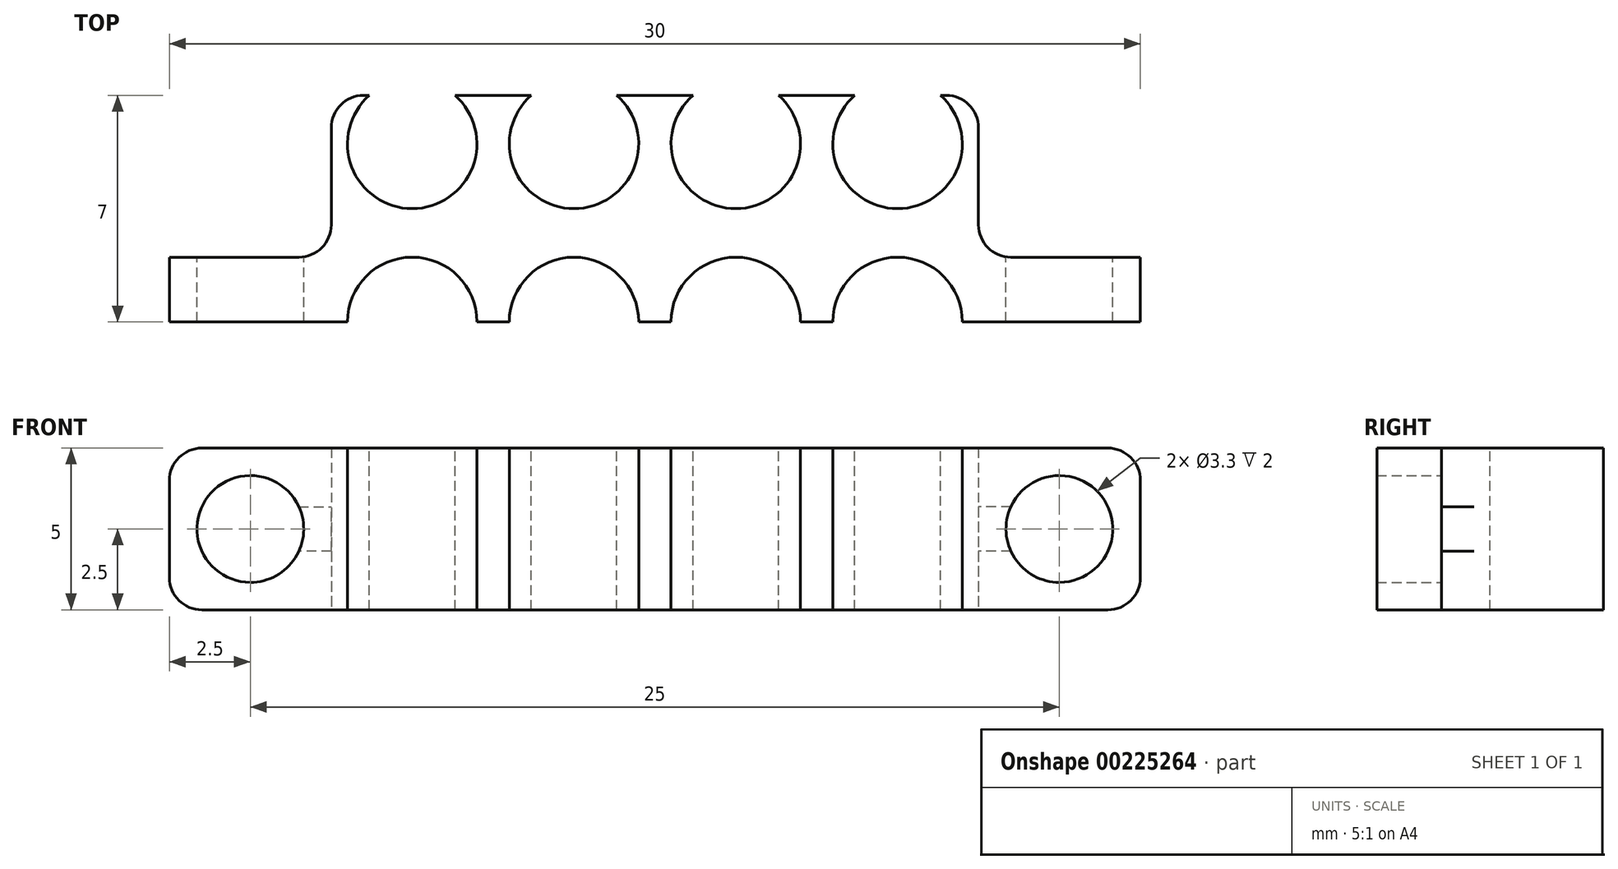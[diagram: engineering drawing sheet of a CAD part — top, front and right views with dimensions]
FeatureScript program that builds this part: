
annotation { "Feature Type Name" : "Feature", "Feature Type Description" : "" }
export const myFeature = defineFeature(function(context is Context, id is Id, definition is map)
    precondition{}
    {
        {
            var Q0;
            Q0=qCreatedBy(makeId("Top.planeOp"),FACE);
            var sketch = newSketch(context, id + "F0", { "sketchPlane" : qUnion([Q0])});
            skLineSegment(sketch, "E0.bottom", {"start": v(-10, 5) * mm, "end": v(10, 5) * mm});
            skLineSegment(sketch, "E0.top", {"start": v(-10, -2) * mm, "end": v(10, -2) * mm});
            skLineSegment(sketch, "E0.left", {"start": v(-10, 5) * mm, "end": v(-10, 0) * mm});
            skLineSegment(sketch, "E0.right", {"start": v(10, 5) * mm, "end": v(10, 0) * mm});
            skLineSegment(sketch, "E1.bottom", {"start": v(-10, -2) * mm, "end": v(-15, -2) * mm});
            skLineSegment(sketch, "E1.top", {"start": v(-10, 0) * mm, "end": v(-15, 0) * mm});
            skLineSegment(sketch, "E1.right", {"start": v(-15, -2) * mm, "end": v(-15, 0) * mm});
            skLineSegment(sketch, "E2.bottom", {"start": v(10, -2) * mm, "end": v(15, -2) * mm});
            skLineSegment(sketch, "E2.top", {"start": v(10, 0) * mm, "end": v(15, 0) * mm});
            skLineSegment(sketch, "E2.right", {"start": v(15, -2) * mm, "end": v(15, 0) * mm});
            skSolve(sketch);
        }
        {
            var Q0;
            Q0 = qSketchRegion(id + "F0", true);
            extrude(context, id + "F1", {"entities" : qUnion([Q0]), "depth" : 5 * mm, "offsetDistance" : 25 * mm});
        }
        {
            var Q0;
            Q0=makeQuery(id+"F1.opExtrude","SWEPT_FACE",FACE,{"disambiguationData":[OSD([sQuery(id+"F0.wireOp",EDGE,"E1.top")])]});
            var sketch = newSketch(context, id + "F2", { "sketchPlane" : qUnion([Q0])});
            skCircle(sketch, "E3", {"center": v(-12.5, 2.5) * mm, "radius": 1.65 * mm});
            skCircle(sketch, "E4", {"center": v(12.5, 2.5) * mm, "radius": 1.65 * mm});
            skPoint(sketch, "E4.centerSnap0", {"position": v(15, 2.5) * mm});
            skSolve(sketch);
        }
        {
            var Q0;
            Q0 = qSketchRegion(id + "F2", true);
            extrude(context, id + "F3", {"entities" : qUnion([Q0]), "operationType" : NewBodyOperationType.REMOVE, "endBound" : BoundingType.THROUGH_ALL, "oppositeDirection" : true, "depth" : 25 * mm, "offsetDistance" : 25 * mm});
        }
        {
            var Q0;
            Q0=makeQuery(id+"F1.opExtrude","CAP_FACE",FACE,{"disambiguationData":[OSD([sQuery(id+"F0.wireOp",EDGE,"E0.bottom"),sQuery(id+"F0.wireOp",EDGE,"E0.top"),sQuery(id+"F0.wireOp",EDGE,"E0.left"),sQuery(id+"F0.wireOp",EDGE,"E0.right"),sQuery(id+"F0.wireOp",EDGE,"E1.bottom"),sQuery(id+"F0.wireOp",EDGE,"E1.top"),sQuery(id+"F0.wireOp",EDGE,"E1.right"),sQuery(id+"F0.wireOp",EDGE,"E2.bottom"),sQuery(id+"F0.wireOp",EDGE,"E2.top"),sQuery(id+"F0.wireOp",EDGE,"E2.right")])],"isStart":false});
            var sketch = newSketch(context, id + "F4", { "sketchPlane" : qUnion([Q0])});
            skArc(sketch, "E5", {"start": v(-5.5, -2) * mm, "mid": v(-7.5, 0) * mm, "end": v(-9.5, -2) * mm});
            skArc(sketch, "E6.1.0.0", {"start": v(-0.5, -2) * mm, "mid": v(-2.5, 0) * mm, "end": v(-4.5, -2) * mm});
            skArc(sketch, "E6.2.0.0", {"start": v(4.5, -2) * mm, "mid": v(2.5, 0) * mm, "end": v(0.5, -2) * mm});
            skArc(sketch, "E6.3.0.0", {"start": v(9.5, -2) * mm, "mid": v(7.5, 0) * mm, "end": v(5.5, -2) * mm});
            skLineSegment(sketch, "E6.direction1", {"start": v(-9.5, -2) * mm, "end": v(-4.5, -2) * mm, "construction": true});
            skLineSegment(sketch, "E7", {"start": v(-12.27, 3.5) * mm, "end": v(13.45, 3.5) * mm, "construction": true});
            skCircle(sketch, "E8", {"center": v(-7.5, 3.5) * mm, "radius": 2 * mm});
            skPoint(sketch, "E8.centerSnap0", {"position": v(-7.5, 0) * mm});
            skCircle(sketch, "E9.1.0.0", {"center": v(-2.5, 3.5) * mm, "radius": 2 * mm});
            skCircle(sketch, "E9.2.0.0", {"center": v(2.5, 3.5) * mm, "radius": 2 * mm});
            skCircle(sketch, "E9.3.0.0", {"center": v(7.5, 3.5) * mm, "radius": 2 * mm});
            skLineSegment(sketch, "E9.direction1", {"start": v(-7.5, 3.5) * mm, "end": v(-2.5, 3.5) * mm, "construction": true});
            skSolve(sketch);
        }
        {
            var Q0;
            {var subQ0=sQuery(id+"F4.wireOp",EDGE,"E5");Q0=makeQuery(id+"F4.imprint","IMPRINT",FACE,{"disambiguationData":[TD([[makeQuery(id+"F4.imprint","IMPRINT",EDGE,{"derivedFrom":subQ0}),1.0]])]});}
            var Q1;
            {var subQ0=sQuery(id+"F4.wireOp",EDGE,"E6.1.0.0");Q1=makeQuery(id+"F4.imprint","IMPRINT",FACE,{"disambiguationData":[TD([[makeQuery(id+"F4.imprint","IMPRINT",EDGE,{"derivedFrom":subQ0}),1.0]])]});}
            var Q2;
            {var subQ0=sQuery(id+"F4.wireOp",EDGE,"E6.2.0.0");Q2=makeQuery(id+"F4.imprint","IMPRINT",FACE,{"disambiguationData":[TD([[makeQuery(id+"F4.imprint","IMPRINT",EDGE,{"derivedFrom":subQ0}),1.0]])]});}
            var Q3;
            {var subQ0=sQuery(id+"F4.wireOp",EDGE,"E6.3.0.0");Q3=makeQuery(id+"F4.imprint","IMPRINT",FACE,{"disambiguationData":[TD([[makeQuery(id+"F4.imprint","IMPRINT",EDGE,{"derivedFrom":subQ0}),1.0]])]});}
            var Q4;
            {var subQ0=sQuery(id+"F4.wireOp",EDGE,"E8");var subQ1=makeQuery(id+"F1.opExtrude","CAP_EDGE",EDGE,{"disambiguationData":[OSD([sQuery(id+"F0.wireOp",EDGE,"E0.bottom")])],"isStart":false});var subQ2=makeQuery(id+"F4.imprint","INTERSECT",VERTEX,{"disambiguationData":[OD(0.0)],"derivedFrom":[subQ1,subQ0]});Q4=makeQuery(id+"F4.imprint","IMPRINT",FACE,{"disambiguationData":[TD([[makeQuery(id+"F4.imprint","IMPRINT",EDGE,{"disambiguationData":[TD([[subQ2,1.0]])],"derivedFrom":subQ0}),1.0]])]});}
            var Q5;
            {var subQ0=sQuery(id+"F4.wireOp",EDGE,"E9.1.0.0");var subQ1=makeQuery(id+"F1.opExtrude","CAP_EDGE",EDGE,{"disambiguationData":[OSD([sQuery(id+"F0.wireOp",EDGE,"E0.bottom")])],"isStart":false});var subQ2=makeQuery(id+"F4.imprint","INTERSECT",VERTEX,{"disambiguationData":[OD(0.0)],"derivedFrom":[subQ1,subQ0]});Q5=makeQuery(id+"F4.imprint","IMPRINT",FACE,{"disambiguationData":[TD([[makeQuery(id+"F4.imprint","IMPRINT",EDGE,{"disambiguationData":[TD([[subQ2,1.0]])],"derivedFrom":subQ0}),1.0]])]});}
            var Q6;
            {var subQ0=sQuery(id+"F4.wireOp",EDGE,"E9.2.0.0");var subQ1=makeQuery(id+"F1.opExtrude","CAP_EDGE",EDGE,{"disambiguationData":[OSD([sQuery(id+"F0.wireOp",EDGE,"E0.bottom")])],"isStart":false});var subQ2=makeQuery(id+"F4.imprint","INTERSECT",VERTEX,{"disambiguationData":[OD(0.0)],"derivedFrom":[subQ1,subQ0]});Q6=makeQuery(id+"F4.imprint","IMPRINT",FACE,{"disambiguationData":[TD([[makeQuery(id+"F4.imprint","IMPRINT",EDGE,{"disambiguationData":[TD([[subQ2,-1.0]])],"derivedFrom":subQ0}),1.0]])]});}
            var Q7;
            {var subQ0=sQuery(id+"F4.wireOp",EDGE,"E9.3.0.0");var subQ1=makeQuery(id+"F1.opExtrude","CAP_EDGE",EDGE,{"disambiguationData":[OSD([sQuery(id+"F0.wireOp",EDGE,"E0.bottom")])],"isStart":false});var subQ2=makeQuery(id+"F4.imprint","INTERSECT",VERTEX,{"disambiguationData":[OD(0.0)],"derivedFrom":[subQ1,subQ0]});Q7=makeQuery(id+"F4.imprint","IMPRINT",FACE,{"disambiguationData":[TD([[makeQuery(id+"F4.imprint","IMPRINT",EDGE,{"disambiguationData":[TD([[subQ2,-1.0]])],"derivedFrom":subQ0}),1.0]])]});}
            var Q8;
            {var subQ0=sQuery(id+"F4.wireOp",EDGE,"E8");var subQ1=makeQuery(id+"F1.opExtrude","CAP_EDGE",EDGE,{"disambiguationData":[OSD([sQuery(id+"F0.wireOp",EDGE,"E0.bottom")])],"isStart":false});var subQ2=makeQuery(id+"F4.imprint","INTERSECT",VERTEX,{"disambiguationData":[OD(0.0)],"derivedFrom":[subQ1,subQ0]});Q8=makeQuery(id+"F4.imprint","IMPRINT",FACE,{"disambiguationData":[TD([[makeQuery(id+"F4.imprint","IMPRINT",EDGE,{"disambiguationData":[TD([[subQ2,-1.0]])],"derivedFrom":subQ0}),1.0]])]});}
            var Q9;
            {var subQ0=sQuery(id+"F4.wireOp",EDGE,"E9.1.0.0");var subQ1=makeQuery(id+"F1.opExtrude","CAP_EDGE",EDGE,{"disambiguationData":[OSD([sQuery(id+"F0.wireOp",EDGE,"E0.bottom")])],"isStart":false});var subQ2=makeQuery(id+"F4.imprint","INTERSECT",VERTEX,{"disambiguationData":[OD(0.0)],"derivedFrom":[subQ1,subQ0]});Q9=makeQuery(id+"F4.imprint","IMPRINT",FACE,{"disambiguationData":[TD([[makeQuery(id+"F4.imprint","IMPRINT",EDGE,{"disambiguationData":[TD([[subQ2,-1.0]])],"derivedFrom":subQ0}),1.0]])]});}
            var Q10;
            {var subQ0=sQuery(id+"F4.wireOp",EDGE,"E9.2.0.0");var subQ1=makeQuery(id+"F1.opExtrude","CAP_EDGE",EDGE,{"disambiguationData":[OSD([sQuery(id+"F0.wireOp",EDGE,"E0.bottom")])],"isStart":false});var subQ2=makeQuery(id+"F4.imprint","INTERSECT",VERTEX,{"disambiguationData":[OD(0.0)],"derivedFrom":[subQ1,subQ0]});Q10=makeQuery(id+"F4.imprint","IMPRINT",FACE,{"disambiguationData":[TD([[makeQuery(id+"F4.imprint","IMPRINT",EDGE,{"disambiguationData":[TD([[subQ2,1.0]])],"derivedFrom":subQ0}),1.0]])]});}
            var Q11;
            {var subQ0=sQuery(id+"F4.wireOp",EDGE,"E9.3.0.0");var subQ1=makeQuery(id+"F1.opExtrude","CAP_EDGE",EDGE,{"disambiguationData":[OSD([sQuery(id+"F0.wireOp",EDGE,"E0.bottom")])],"isStart":false});var subQ2=makeQuery(id+"F4.imprint","INTERSECT",VERTEX,{"disambiguationData":[OD(0.0)],"derivedFrom":[subQ1,subQ0]});Q11=makeQuery(id+"F4.imprint","IMPRINT",FACE,{"disambiguationData":[TD([[makeQuery(id+"F4.imprint","IMPRINT",EDGE,{"disambiguationData":[TD([[subQ2,1.0]])],"derivedFrom":subQ0}),1.0]])]});}
            extrude(context, id + "F5", {"entities" : qUnion([Q0, Q1, Q2, Q3, Q4, Q5, Q6, Q7, Q8, Q9, Q10, Q11]), "operationType" : NewBodyOperationType.REMOVE, "endBound" : BoundingType.UP_TO_NEXT, "oppositeDirection" : true, "depth" : 25 * mm, "offsetDistance" : 25 * mm});
        }
        {
            var Q0;
            Q0=makeQuery(id+"F1.opExtrude","SWEPT_EDGE",EDGE,{"disambiguationData":[OSD([sQuery(id+"F0.wireOp",EDGE,"E0.left"),sQuery(id+"F0.wireOp",EDGE,"E1.top")])]});
            var Q1;
            Q1=makeQuery(id+"F1.opExtrude","SWEPT_EDGE",EDGE,{"disambiguationData":[OSD([sQuery(id+"F0.wireOp",EDGE,"E0.right"),sQuery(id+"F0.wireOp",EDGE,"E2.top")])]});
            var Q2;
            Q2=makeQuery(id+"F1.opExtrude","SWEPT_EDGE",EDGE,{"disambiguationData":[OSD([sQuery(id+"F0.wireOp",EDGE,"E0.bottom"),sQuery(id+"F0.wireOp",EDGE,"E0.right")])]});
            var Q3;
            Q3=makeQuery(id+"F1.opExtrude","SWEPT_EDGE",EDGE,{"disambiguationData":[OSD([sQuery(id+"F0.wireOp",EDGE,"E0.bottom"),sQuery(id+"F0.wireOp",EDGE,"E0.left")])]});
            var Q4;
            Q4=makeQuery(id+"F1.opExtrude","CAP_EDGE",EDGE,{"disambiguationData":[OSD([sQuery(id+"F0.wireOp",EDGE,"E2.right")])],"isStart":false});
            var Q5;
            Q5=makeQuery(id+"F1.opExtrude","CAP_EDGE",EDGE,{"disambiguationData":[OSD([sQuery(id+"F0.wireOp",EDGE,"E2.right")])],"isStart":true});
            var Q6;
            Q6=makeQuery(id+"F1.opExtrude","CAP_EDGE",EDGE,{"disambiguationData":[OSD([sQuery(id+"F0.wireOp",EDGE,"E1.right")])],"isStart":true});
            var Q7;
            Q7=makeQuery(id+"F1.opExtrude","CAP_EDGE",EDGE,{"disambiguationData":[OSD([sQuery(id+"F0.wireOp",EDGE,"E1.right")])],"isStart":false});
            fillet(context, id + "F6", {"entities" : qUnion([Q0, Q1, Q2, Q3, Q4, Q5, Q6, Q7]), "radius" : 1 * mm, "tangentPropagation" : true, "allowEdgeOverflow" : false});
        }
    });
